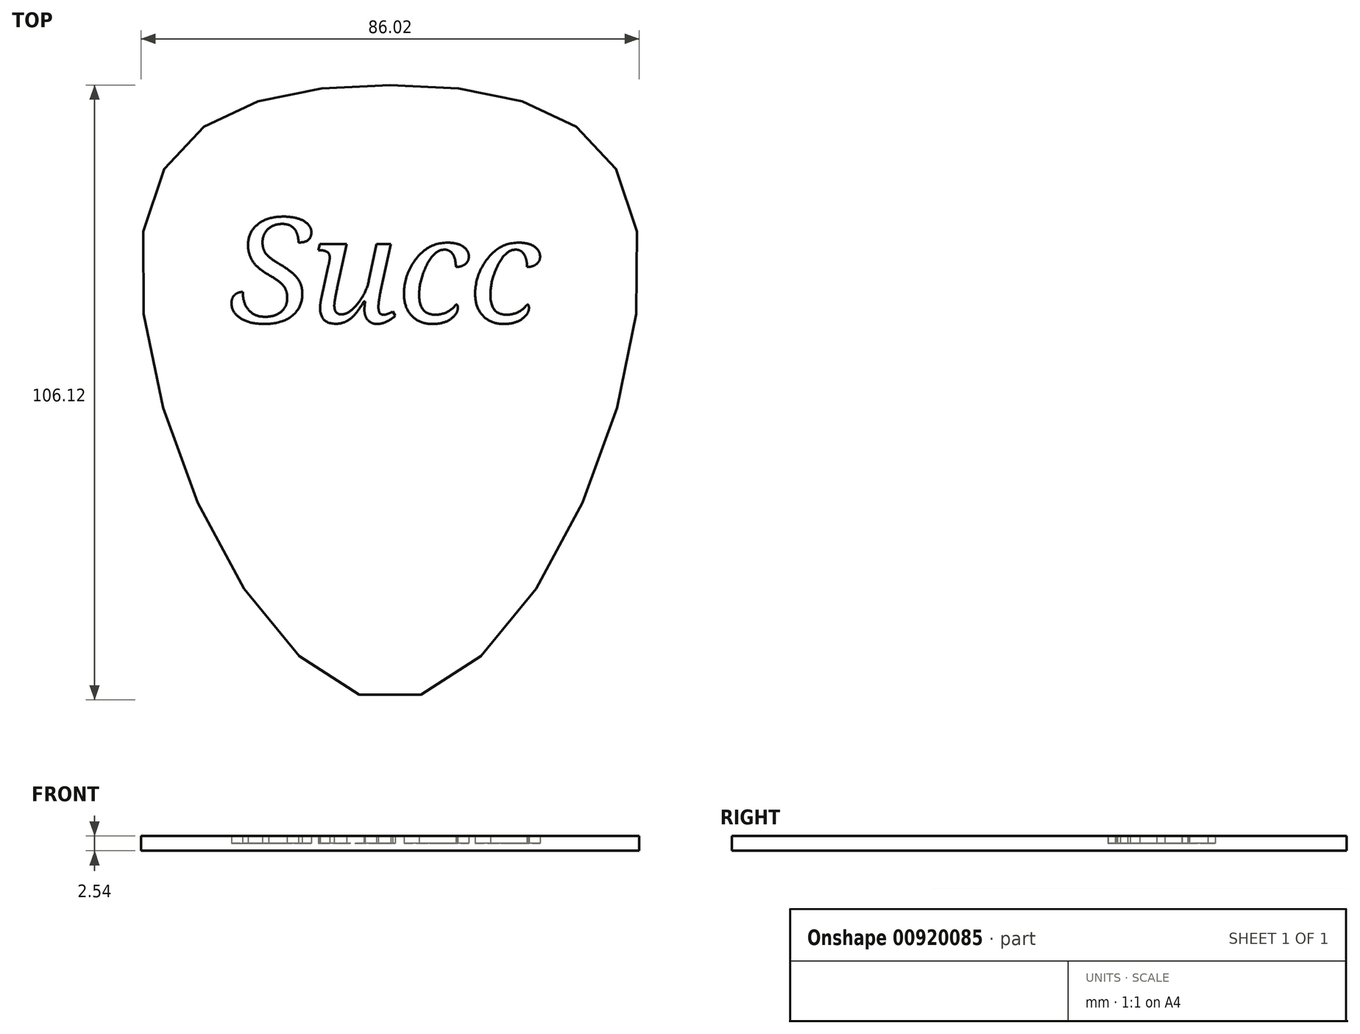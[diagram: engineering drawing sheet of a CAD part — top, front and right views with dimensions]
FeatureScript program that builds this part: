
annotation { "Feature Type Name" : "Feature", "Feature Type Description" : "" }
export const myFeature = defineFeature(function(context is Context, id is Id, definition is map)
    precondition{}
    {
        {
            var Q0;
            Q0=qCreatedBy(makeId("Top.planeOp"),FACE);
            var sketch = newSketch(context, id + "F0", { "sketchPlane" : qUnion([Q0])});
            skFitSpline(sketch, "E0", {"points": [v(0, 22.8) * mm, v(42.2, 0) * mm, v(0, -83.33) * mm, v(-42.2, 0) * mm, v(0, 22.8) * mm]});
            skText(sketch, "E1", { "text": "Succ", "fontName": "NotoSerif-Italic.ttf"});
            const initialGuessF0  = {"E1": [-0.02755, -0.01818, 1, 0, 0.01818]};
            skSetInitialGuess(sketch, initialGuessF0);
            skSolve(sketch);
        }
        {
            var Q0;
            Q0=makeQuery(id+"F0.imprint","IMPRINT",FACE,{"disambiguationData":[TD([[makeQuery(id+"F0.imprint","IMPRINT",EDGE,{"derivedFrom":sQuery(id+"F0.wireOp",EDGE,"E0")}),-1.0]])]});
            var Q1;
            Q1=makeQuery(id+"F0.imprint","IMPRINT",FACE,{"disambiguationData":[TD([[makeQuery(id+"F0.imprint","IMPRINT",EDGE,{"derivedFrom":sQuery(id+"F0.wireOp",EDGE,"E1.sketch_text.stroke-0")}),-1.0]])]});
            var Q2;
            Q2=makeQuery(id+"F0.imprint","IMPRINT",FACE,{"disambiguationData":[TD([[makeQuery(id+"F0.imprint","IMPRINT",EDGE,{"derivedFrom":sQuery(id+"F0.wireOp",EDGE,"E1.sketch_text.stroke-27")}),-1.0]])]});
            var Q3;
            Q3=makeQuery(id+"F0.imprint","IMPRINT",FACE,{"disambiguationData":[TD([[makeQuery(id+"F0.imprint","IMPRINT",EDGE,{"derivedFrom":sQuery(id+"F0.wireOp",EDGE,"E1.sketch_text.stroke-54")}),-1.0]])]});
            var Q4;
            Q4=makeQuery(id+"F0.imprint","IMPRINT",FACE,{"disambiguationData":[TD([[makeQuery(id+"F0.imprint","IMPRINT",EDGE,{"derivedFrom":sQuery(id+"F0.wireOp",EDGE,"E1.sketch_text.stroke-71")}),-1.0]])]});
            extrude(context, id + "F1", {"entities" : qUnion([Q0, Q1, Q2, Q3, Q4]), "oppositeDirection" : true, "depth" : 1.27 * mm, "offsetDistance" : 25.4 * mm});
        }
        {
            var Q0;
            Q0=makeQuery(id+"F0.imprint","IMPRINT",FACE,{"disambiguationData":[TD([[makeQuery(id+"F0.imprint","IMPRINT",EDGE,{"derivedFrom":sQuery(id+"F0.wireOp",EDGE,"E0")}),-1.0]])]});
            extrude(context, id + "F2", {"entities" : qUnion([Q0]), "operationType" : NewBodyOperationType.ADD, "depth" : 1.27 * mm, "offsetDistance" : 25.4 * mm});
        }
    });
